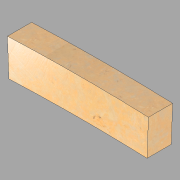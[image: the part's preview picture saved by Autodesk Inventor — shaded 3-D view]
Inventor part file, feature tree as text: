
AUTODESK INVENTOR PART (.ipt)
format: ipt  version: 2022.1 (Build 261234020, 234B)  size: 109,568 bytes
history: imported  units: in
note: dims shown in document units (in); Inventor stores cm internally (conversion verified against a paired STEP export)
features: imported_body x1
ambient origin geometry x8: Origin, YZ Plane, XZ Plane, XY Plane, X Axis, Y Axis, Z Axis, Center Point
bodies: Solid1 (imported_parasolid), Body1 (imported_parasolid)
feature tree (1):
  imported_body  NMx_Import_Brep_tag  [imported B-rep: ~7 faces, bbox_mm=[889.31347, 231.163309, 152.4]]
